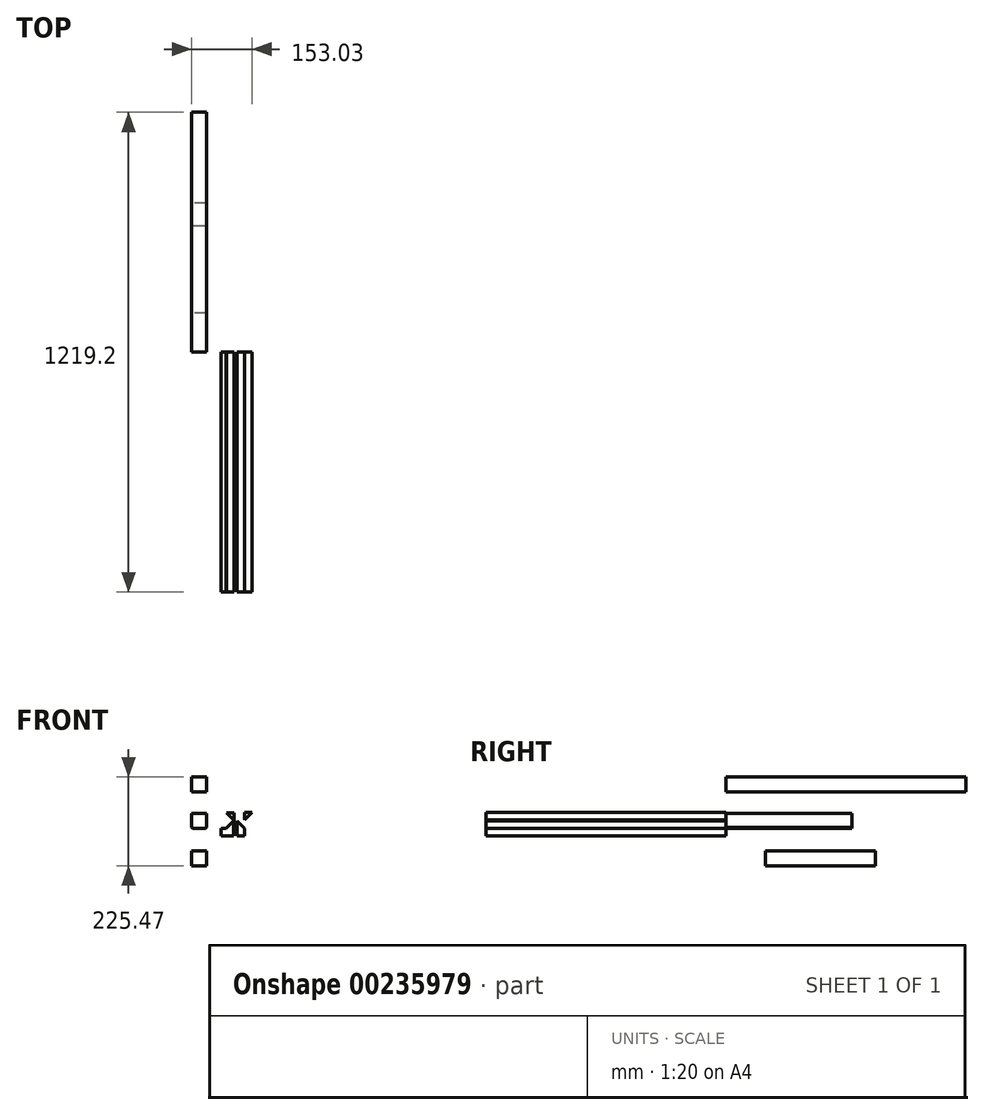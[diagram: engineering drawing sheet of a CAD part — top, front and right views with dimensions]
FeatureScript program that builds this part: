
annotation { "Feature Type Name" : "Feature", "Feature Type Description" : "" }
export const myFeature = defineFeature(function(context is Context, id is Id, definition is map)
    precondition{}
    {
        {
            var Q0;
            Q0=qCreatedBy(makeId("Right.planeOp"),FACE);
            var sketch = newSketch(context, id + "F0", { "sketchPlane" : qUnion([Q0])});
            skLineSegment(sketch, "E0.bottom", {"start": v(0, 0) * mm, "end": v(320.68, 0) * mm});
            skLineSegment(sketch, "E0.top", {"start": v(0, 38.1) * mm, "end": v(320.68, 38.1) * mm});
            skLineSegment(sketch, "E0.left", {"start": v(0, 0) * mm, "end": v(0, 38.1) * mm});
            skLineSegment(sketch, "E0.right", {"start": v(320.68, 0) * mm, "end": v(320.68, 38.1) * mm});
            skSolve(sketch);
        }
        {
            var Q0;
            Q0 = qSketchRegion(id + "F0", true);
            extrude(context, id + "F1", {"entities" : qUnion([Q0]), "depth" : 38.1 * mm});
        }
        {
            var Q0;
            Q0=makeQuery(id+"F1.opExtrude","CAP_EDGE",EDGE,{"disambiguationData":[OSD([sQuery(id+"F0.wireOp",EDGE,"E0.bottom")])],"isStart":false});
            var Q1;
            Q1=makeQuery(id+"F1.opExtrude","CAP_EDGE",EDGE,{"disambiguationData":[OSD([sQuery(id+"F0.wireOp",EDGE,"E0.bottom")])],"isStart":true});
            chamfer(context, id + "F2", {"entities" : qUnion([Q0, Q1]), "width" : 2.54 * mm, "tangentPropagation" : true});
        }
        {
            var Q0;
            Q0=qCreatedBy(makeId("Right.planeOp"),FACE);
            var sketch = newSketch(context, id + "F3", { "sketchPlane" : qUnion([Q0])});
            skLineSegment(sketch, "E1.bottom", {"start": v(0, 92.27) * mm, "end": v(609.6, 92.27) * mm});
            skLineSegment(sketch, "E1.top", {"start": v(0, 130.37) * mm, "end": v(609.6, 130.37) * mm});
            skLineSegment(sketch, "E1.left", {"start": v(0, 92.27) * mm, "end": v(0, 130.37) * mm});
            skLineSegment(sketch, "E1.right", {"start": v(609.6, 92.27) * mm, "end": v(609.6, 130.37) * mm});
            skSolve(sketch);
        }
        {
            var Q0;
            Q0 = qSketchRegion(id + "F3", true);
            extrude(context, id + "F4", {"entities" : qUnion([Q0]), "depth" : 38.1 * mm});
        }
        {
            var Q0;
            Q0=qCreatedBy(makeId("Right.planeOp"),FACE);
            var sketch = newSketch(context, id + "F5", { "sketchPlane" : qUnion([Q0])});
            skLineSegment(sketch, "E2.bottom", {"start": v(99.9, -57) * mm, "end": v(379.3, -57) * mm});
            skLineSegment(sketch, "E2.top", {"start": v(99.9, -95.1) * mm, "end": v(379.3, -95.1) * mm});
            skLineSegment(sketch, "E2.left", {"start": v(99.9, -57) * mm, "end": v(99.9, -95.1) * mm});
            skLineSegment(sketch, "E2.right", {"start": v(379.3, -57) * mm, "end": v(379.3, -95.1) * mm});
            skSolve(sketch);
        }
        {
            var Q0;
            Q0 = qSketchRegion(id + "F5", true);
            extrude(context, id + "F6", {"entities" : qUnion([Q0]), "depth" : 38.1 * mm});
        }
        {
            var Q0;
            Q0=qCreatedBy(makeId("Front.planeOp"),FACE);
            var sketch = newSketch(context, id + "F7", { "sketchPlane" : qUnion([Q0])});
            skLineSegment(sketch, "E3.top", {"start": v(114.99, 0) * mm, "end": v(134.04, 0) * mm});
            skLineSegment(sketch, "E3.left", {"start": v(114.99, 19.05) * mm, "end": v(114.99, 0) * mm});
            skLineSegment(sketch, "E4.top", {"start": v(114.99, -19.05) * mm, "end": v(134.04, -19.05) * mm});
            skLineSegment(sketch, "E4.left", {"start": v(114.99, 0) * mm, "end": v(114.99, -19.05) * mm});
            skLineSegment(sketch, "E4.right", {"start": v(134.04, 0) * mm, "end": v(134.04, -19.05) * mm});
            skLineSegment(sketch, "E5", {"start": v(114.99, 19.05) * mm, "end": v(134.04, 0) * mm});
            skSolve(sketch);
        }
        {
            var Q0;
            Q0 = qSketchRegion(id + "F7", true);
            extrude(context, id + "F8", {"entities" : qUnion([Q0]), "depth" : 609.6 * mm});
        }
        {
            var Q0;
            Q0=qCreatedBy(makeId("Front.planeOp"),FACE);
            var sketch = newSketch(context, id + "F9", { "sketchPlane" : qUnion([Q0])});
            skLineSegment(sketch, "E6.bottom", {"start": v(87.54, -19.05) * mm, "end": v(106.59, -19.05) * mm});
            skLineSegment(sketch, "E6.left", {"start": v(87.54, -19.05) * mm, "end": v(87.54, 0) * mm});
            skLineSegment(sketch, "E6.right", {"start": v(106.59, -19.05) * mm, "end": v(106.59, 0) * mm});
            skLineSegment(sketch, "E7", {"start": v(106.59, 0) * mm, "end": v(106.59, 19.05) * mm});
            skLineSegment(sketch, "E8", {"start": v(106.59, 19.05) * mm, "end": v(87.54, 0) * mm});
            skLineSegment(sketch, "E9.bottom", {"start": v(87.54, -19.05) * mm, "end": v(74.84, -19.05) * mm});
            skLineSegment(sketch, "E9.top", {"start": v(87.54, 0) * mm, "end": v(74.84, 0) * mm});
            skLineSegment(sketch, "E9.right", {"start": v(74.84, -19.05) * mm, "end": v(74.84, 0) * mm});
            skSolve(sketch);
        }
        {
            var Q0;
            Q0 = qSketchRegion(id + "F9", true);
            extrude(context, id + "F10", {"entities" : qUnion([Q0]), "depth" : 609.6 * mm});
        }
        {
            var Q0;
            Q0=qCreatedBy(makeId("Front.planeOp"),FACE);
            var sketch = newSketch(context, id + "F11", { "sketchPlane" : qUnion([Q0])});
            skLineSegment(sketch, "E10", {"start": v(88.25, 39.12) * mm, "end": v(107.3, 39.12) * mm});
            skLineSegment(sketch, "E11", {"start": v(107.3, 39.12) * mm, "end": v(107.3, 20.07) * mm});
            skLineSegment(sketch, "E12", {"start": v(107.3, 20.07) * mm, "end": v(88.25, 39.12) * mm});
            skSolve(sketch);
        }
        {
            var Q0;
            Q0=makeQuery(id+"F11.imprint","IMPRINT",FACE,{"disambiguationData":[TD([[makeQuery(id+"F11.imprint","IMPRINT",EDGE,{"derivedFrom":sQuery(id+"F11.wireOp",EDGE,"E10")}),-1.0]])]});
            extrude(context, id + "F12", {"entities" : qUnion([Q0]), "depth" : 609.6 * mm});
        }
        {
            var Q0;
            Q0=qCreatedBy(makeId("Front.planeOp"),FACE);
            var sketch = newSketch(context, id + "F13", { "sketchPlane" : qUnion([Q0])});
            skLineSegment(sketch, "E13", {"start": v(133.98, 40.07) * mm, "end": v(133.98, 21.02) * mm});
            skLineSegment(sketch, "E14", {"start": v(133.98, 40.07) * mm, "end": v(153.03, 40.07) * mm});
            skLineSegment(sketch, "E15", {"start": v(153.03, 40.07) * mm, "end": v(133.98, 21.02) * mm});
            skSolve(sketch);
        }
        {
            var Q0;
            Q0 = qSketchRegion(id + "F13", true);
            extrude(context, id + "F14", {"entities" : qUnion([Q0]), "depth" : 609.6 * mm});
        }
    });
